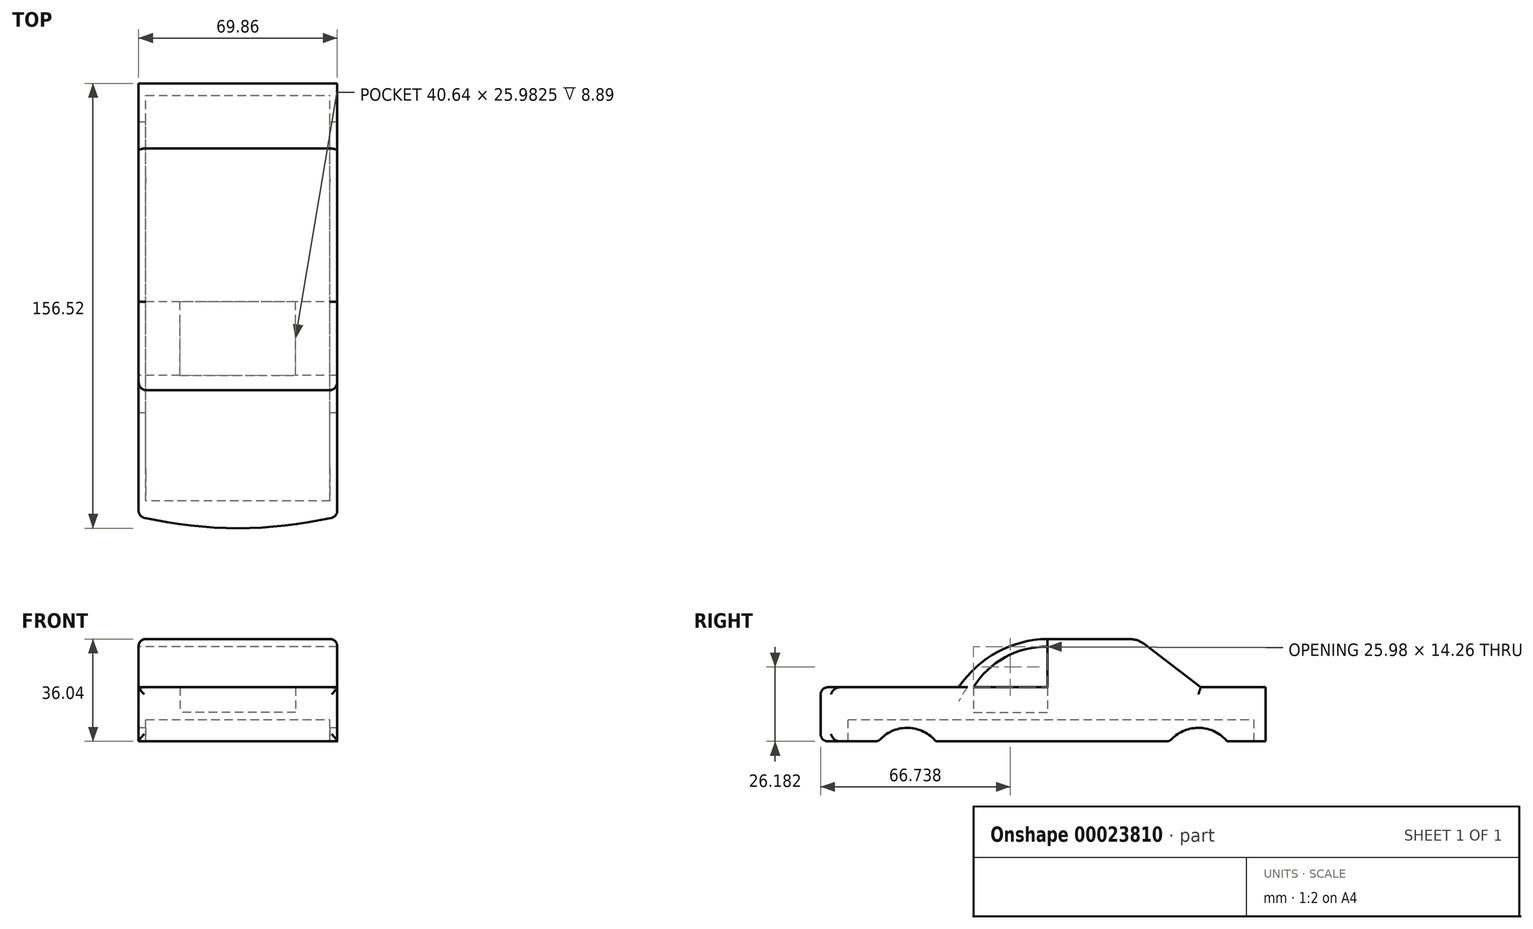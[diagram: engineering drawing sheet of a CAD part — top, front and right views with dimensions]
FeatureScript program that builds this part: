
annotation { "Feature Type Name" : "Feature", "Feature Type Description" : "" }
export const myFeature = defineFeature(function(context is Context, id is Id, definition is map)
    precondition{}
    {
        {
            var Q0;
            Q0=qCreatedBy(makeId("Top.planeOp"),FACE);
            var sketch = newSketch(context, id + "F0", { "sketchPlane" : qUnion([Q0])});
            skArc(sketch, "E0", {"start": v(-34.92, -38.6) * mm, "mid": v(0, -42.72) * mm, "end": v(34.93, -38.6) * mm});
            skPoint(sketch, "E1", {"position": v(0, -38.44) * mm});
            skLineSegment(sketch, "E2", {"start": v(-34.92, -38.6) * mm, "end": v(-34.92, 5.85) * mm});
            skLineSegment(sketch, "E3", {"start": v(-34.92, 5.85) * mm, "end": v(34.93, 5.85) * mm});
            skLineSegment(sketch, "E4", {"start": v(34.93, 5.85) * mm, "end": v(34.93, -38.6) * mm});
            skLineSegment(sketch, "E5", {"start": v(-76.26, -38.6) * mm, "end": v(76.46, -38.6) * mm, "construction": true});
            skSolve(sketch);
        }
        {
            var Q0;
            Q0 = qSketchRegion(id + "F0", true);
            extrude(context, id + "F1", {"entities" : qUnion([Q0]), "depth" : 6.35 * mm, "hasSecondDirection" : true, "secondDirectionOppositeDirection" : true, "secondDirectionDepth" : 12.7 * mm});
        }
        {
            var Q0;
            Q0=qCreatedBy(makeId("Right.planeOp"),FACE);
            var sketch = newSketch(context, id + "F2", { "sketchPlane" : qUnion([Q0])});
            skArc(sketch, "E6", {"start": v(37, 23.34) * mm, "mid": v(19.33, 18.7) * mm, "end": v(5.85, 6.35) * mm});
            skLineSegment(sketch, "E7", {"start": v(37, 23.34) * mm, "end": v(68.76, 23.34) * mm});
            skLineSegment(sketch, "E8", {"start": v(68.76, 23.34) * mm, "end": v(90.94, 6.35) * mm});
            skLineSegment(sketch, "E9", {"start": v(90.94, 6.35) * mm, "end": v(113.8, 6.35) * mm});
            skLineSegment(sketch, "E10", {"start": v(113.8, -12.7) * mm, "end": v(5.85, -12.7) * mm});
            skLineSegment(sketch, "E11", {"start": v(5.85, -12.7) * mm, "end": v(5.85, 6.35) * mm});
            skLineSegment(sketch, "E12", {"start": v(113.8, 6.35) * mm, "end": v(113.8, -12.7) * mm});
            skSolve(sketch);
        }
        {
            var Q0;
            Q0 = qSketchRegion(id + "F2", true);
            extrude(context, id + "F3", {"entities" : qUnion([Q0]), "operationType" : NewBodyOperationType.ADD, "depth" : 34.92 * mm, "hasSecondDirection" : true, "secondDirectionOppositeDirection" : true, "secondDirectionDepth" : 34.92 * mm});
        }
        {
            var Q0;
            Q0=makeQuery(id+"F3.opExtrude","CAP_FACE",FACE,{"disambiguationData":[OSD([sQuery(id+"F2.wireOp",EDGE,"E6"),sQuery(id+"F2.wireOp",EDGE,"E7"),sQuery(id+"F2.wireOp",EDGE,"E8"),sQuery(id+"F2.wireOp",EDGE,"E9"),sQuery(id+"F2.wireOp",EDGE,"E10"),sQuery(id+"F2.wireOp",EDGE,"E11"),sQuery(id+"F2.wireOp",EDGE,"E12")])],"isStart":true});
            var sketch = newSketch(context, id + "F4", { "sketchPlane" : qUnion([Q0])});
            skArc(sketch, "E13", {"start": v(-11.03, 6.35) * mm, "mid": v(-22.12, 16.93) * mm, "end": v(-37, 20.61) * mm});
            skLineSegment(sketch, "E14", {"start": v(-37, 20.61) * mm, "end": v(-37, 6.35) * mm});
            skLineSegment(sketch, "E15", {"start": v(-37, 6.35) * mm, "end": v(-11.03, 6.35) * mm});
            skSolve(sketch);
        }
        {
            var Q0;
            Q0 = qSketchRegion(id + "F4", true);
            extrude(context, id + "F5", {"entities" : qUnion([Q0]), "operationType" : NewBodyOperationType.REMOVE, "endBound" : BoundingType.THROUGH_ALL, "oppositeDirection" : true, "depth" : 25.4 * mm});
        }
        {
            var Q0;
            Q0=qCreatedBy(makeId("Right.planeOp"),FACE);
            var sketch = newSketch(context, id + "F6", { "sketchPlane" : qUnion([Q0])});
            skLineSegment(sketch, "E16.bottom", {"start": v(37, 6.35) * mm, "end": v(11.03, 6.35) * mm});
            skLineSegment(sketch, "E16.top", {"start": v(37, -8.9) * mm, "end": v(11.03, -8.9) * mm});
            skLineSegment(sketch, "E16.left", {"start": v(37, 6.35) * mm, "end": v(37, -8.9) * mm});
            skLineSegment(sketch, "E16.right", {"start": v(11.03, 6.35) * mm, "end": v(11.03, -8.9) * mm});
            skSolve(sketch);
        }
        {
            var Q0;
            Q0 = qSketchRegion(id + "F6", true);
            extrude(context, id + "F7", {"entities" : qUnion([Q0]), "operationType" : NewBodyOperationType.REMOVE, "oppositeDirection" : true, "depth" : 20.32 * mm, "hasSecondDirection" : true, "secondDirectionOppositeDirection" : false, "secondDirectionDepth" : 20.32 * mm});
        }
        {
            var Q0;
            Q0=makeQuery(id+"F3.opExtrude","CAP_FACE",FACE,{"disambiguationData":[OSD([sQuery(id+"F2.wireOp",EDGE,"E6"),sQuery(id+"F2.wireOp",EDGE,"E7"),sQuery(id+"F2.wireOp",EDGE,"E8"),sQuery(id+"F2.wireOp",EDGE,"E9"),sQuery(id+"F2.wireOp",EDGE,"E10"),sQuery(id+"F2.wireOp",EDGE,"E11"),sQuery(id+"F2.wireOp",EDGE,"E12")])],"isStart":true});
            var sketch = newSketch(context, id + "F8", { "sketchPlane" : qUnion([Q0])});
            skArc(sketch, "E17", {"start": v(-80.04, -12.7) * mm, "mid": v(-90.12, -7.94) * mm, "end": v(-100.2, -12.7) * mm});
            skSolve(sketch);
        }
        {
            var Q0;
            {var subQ1=sQuery(id+"F8.wireOp",EDGE,"E17");Q0=makeQuery(id+"F8.imprint","IMPRINT",FACE,{"disambiguationData":[TD([[makeQuery(id+"F8.imprint","IMPRINT",EDGE,{"derivedFrom":subQ1}),1.0]])]});}
            extrude(context, id + "F9", {"entities" : qUnion([Q0]), "operationType" : NewBodyOperationType.REMOVE, "endBound" : BoundingType.THROUGH_ALL, "oppositeDirection" : true, "depth" : 25.4 * mm});
        }
        {
            var Q0;
            Q0=makeQuery(id+"F1.opExtrude","SWEPT_FACE",FACE,{"disambiguationData":[OSD([sQuery(id+"F0.wireOp",EDGE,"E2")])]});
            var sketch = newSketch(context, id + "F10", { "sketchPlane" : qUnion([Q0])});
            skArc(sketch, "E18", {"start": v(22.36, -12.7) * mm, "mid": v(12.28, -7.94) * mm, "end": v(2.2, -12.7) * mm});
            skSolve(sketch);
        }
        {
            var Q0;
            {var subQ1=sQuery(id+"F10.wireOp",EDGE,"E18");Q0=makeQuery(id+"F10.imprint","IMPRINT",FACE,{"disambiguationData":[TD([[makeQuery(id+"F10.imprint","IMPRINT",EDGE,{"derivedFrom":subQ1}),1.0]])]});}
            extrude(context, id + "F11", {"entities" : qUnion([Q0]), "operationType" : NewBodyOperationType.REMOVE, "endBound" : BoundingType.THROUGH_ALL, "oppositeDirection" : true, "depth" : 25.4 * mm});
        }
        {
            var Q0;
            {var subQ0=sQuery(id+"F0.wireOp",EDGE,"E0");var subQ1=sQuery(id+"F0.wireOp",EDGE,"E2");var subQ2=sQuery(id+"F0.wireOp",EDGE,"E4");var subQ3=sQuery(id+"F2.wireOp",EDGE,"E10");var subQ4=makeQuery(id+"F9.opExtrude","SWEPT_FACE",FACE,{"disambiguationData":[OSD([sQuery(id+"F8.wireOp",EDGE,"E17")])]});Q0=makeQuery(id+"F11.boolean.opBoolean","SPLIT",FACE,{"disambiguationData":[TD([makeQuery(id+"F9.boolean.opBoolean","COPY",FACE,{"derivedFrom":subQ4})])],"derivedFrom":makeQuery(id+"F9.boolean.opBoolean","SPLIT",FACE,{"disambiguationData":[TD([makeQuery(id+"F1.opExtrude","SWEPT_FACE",FACE,{"disambiguationData":[OSD([subQ0])]})])],"derivedFrom":makeQuery(id+"F3.boolean.opBoolean","MERGE",FACE,{"derivedFrom":[makeQuery(id+"F1.opExtrude","CAP_FACE",FACE,{"disambiguationData":[OSD([subQ0,subQ1,sQuery(id+"F0.wireOp",EDGE,"E3"),subQ2])],"isStart":true}),makeQuery(id+"F3.opExtrude","SWEPT_FACE",FACE,{"disambiguationData":[OSD([subQ3])]})]})})});}
            var sketch = newSketch(context, id + "F12", { "sketchPlane" : qUnion([Q0])});
            skLineSegment(sketch, "E19.left", {"start": v(32.38, 5.25) * mm, "end": v(32.39, -83.09) * mm});
            skLineSegment(sketch, "E19.right", {"start": v(-32.39, 5.25) * mm, "end": v(-32.38, -83.09) * mm});
            skLineSegment(sketch, "E20", {"start": v(-32.39, 5.25) * mm, "end": v(32.38, 5.25) * mm});
            skLineSegment(sketch, "E21", {"start": v(-32.38, -83.09) * mm, "end": v(32.39, -83.09) * mm});
            skSolve(sketch);
        }
        {
            var Q0;
            Q0 = qSketchRegion(id + "F12", true);
            extrude(context, id + "F13", {"entities" : qUnion([Q0]), "operationType" : NewBodyOperationType.REMOVE, "oppositeDirection" : true, "depth" : 7.62 * mm});
        }
        {
            var Q0;
            Q0=makeQuery(id+"F3.opExtrude","CAP_EDGE",EDGE,{"disambiguationData":[OSD([sQuery(id+"F2.wireOp",EDGE,"E7")])],"isStart":true});
            var Q1;
            Q1=makeQuery(id+"F3.opExtrude","CAP_EDGE",EDGE,{"disambiguationData":[OSD([sQuery(id+"F2.wireOp",EDGE,"E7")])],"isStart":false});
            var Q2;
            Q2=makeQuery(id+"F3.opExtrude","CAP_EDGE",EDGE,{"disambiguationData":[OSD([sQuery(id+"F2.wireOp",EDGE,"E8")])],"isStart":false});
            var Q3;
            Q3=makeQuery(id+"F3.opExtrude","CAP_EDGE",EDGE,{"disambiguationData":[OSD([sQuery(id+"F2.wireOp",EDGE,"E8")])],"isStart":true});
            var Q4;
            Q4=makeQuery(id+"F3.opExtrude","CAP_EDGE",EDGE,{"disambiguationData":[OSD([sQuery(id+"F2.wireOp",EDGE,"E9")])],"isStart":true});
            var Q5;
            Q5=makeQuery(id+"F3.opExtrude","CAP_EDGE",EDGE,{"disambiguationData":[OSD([sQuery(id+"F2.wireOp",EDGE,"E9")])],"isStart":false});
            fillet(context, id + "F14", {"entities" : qUnion([Q0, Q1, Q2, Q3, Q4, Q5]), "radius" : 2.54 * mm, "tangentPropagation" : true, "allowEdgeOverflow" : false});
        }
        {
            var Q0;
            Q0=makeQuery(id+"F3.opExtrude","SWEPT_EDGE",EDGE,{"disambiguationData":[OSD([sQuery(id+"F2.wireOp",EDGE,"E7"),sQuery(id+"F2.wireOp",EDGE,"E8")])]});
            fillet(context, id + "F15", {"entities" : qUnion([Q0]), "radius" : 8.9 * mm, "tangentPropagation" : true, "allowEdgeOverflow" : false});
        }
        {
            var Q0;
            Q0=makeQuery(id+"F3.opExtrude","CAP_EDGE",EDGE,{"disambiguationData":[OSD([sQuery(id+"F2.wireOp",EDGE,"E6")])],"isStart":true});
            fillet(context, id + "F16", {"entities" : qUnion([Q0]), "radius" : 2.54 * mm, "tangentPropagation" : true, "allowEdgeOverflow" : false});
        }
        {
            var Q0;
            Q0=makeQuery(id+"F1.opExtrude","CAP_EDGE",EDGE,{"disambiguationData":[OSD([sQuery(id+"F0.wireOp",EDGE,"E0")])],"isStart":false});
            var Q1;
            Q1=makeQuery(id+"F1.opExtrude","SWEPT_EDGE",EDGE,{"disambiguationData":[OSD([sQuery(id+"F0.wireOp",EDGE,"E0"),sQuery(id+"F0.wireOp",EDGE,"E2")])]});
            var Q2;
            Q2=makeQuery(id+"F1.opExtrude","SWEPT_EDGE",EDGE,{"disambiguationData":[OSD([sQuery(id+"F0.wireOp",EDGE,"E0"),sQuery(id+"F0.wireOp",EDGE,"E4")])]});
            var Q3;
            Q3=makeQuery(id+"F1.opExtrude","CAP_EDGE",EDGE,{"disambiguationData":[OSD([sQuery(id+"F0.wireOp",EDGE,"E0")])],"isStart":true});
            var Q4;
            {var subQ0=sQuery(id+"F0.wireOp",EDGE,"E2");var subQ1=sQuery(id+"F10.wireOp",EDGE,"E18");Q4=makeQuery(id+"F11.boolean.opBoolean","COPY",EDGE,{"derivedFrom":makeQuery(id+"F11.opExtrude","SWEPT_EDGE",EDGE,{"disambiguationData":[OSD([subQ0,subQ1]),TDD([makeQuery(id+"F10.imprint","INTERSECT",VERTEX,{"disambiguationData":[OD(0.0)],"derivedFrom":[makeQuery(id+"F1.opExtrude","CAP_EDGE",EDGE,{"disambiguationData":[OSD([subQ0])],"isStart":true}),subQ1]})])]})});}
            var Q5;
            Q5=makeQuery(id+"F13.boolean.opBoolean","INTERSECT",EDGE,{"derivedFrom":[makeQuery(id+"F11.boolean.opBoolean","COPY",FACE,{"derivedFrom":makeQuery(id+"F11.opExtrude","SWEPT_FACE",FACE,{"disambiguationData":[OSD([sQuery(id+"F10.wireOp",EDGE,"E18")])]})}),makeQuery(id+"F13.opExtrude","SWEPT_FACE",FACE,{"disambiguationData":[OSD([sQuery(id+"F12.wireOp",EDGE,"E20")])]})]});
            var Q6;
            Q6=makeQuery(id+"F13.boolean.opBoolean","INTERSECT",EDGE,{"derivedFrom":[makeQuery(id+"F9.boolean.opBoolean","COPY",FACE,{"derivedFrom":makeQuery(id+"F9.opExtrude","SWEPT_FACE",FACE,{"disambiguationData":[OSD([sQuery(id+"F8.wireOp",EDGE,"E17")])]})}),makeQuery(id+"F13.opExtrude","SWEPT_FACE",FACE,{"disambiguationData":[OSD([sQuery(id+"F12.wireOp",EDGE,"E21")])]})]});
            var Q7;
            {var subQ0=sQuery(id+"F2.wireOp",EDGE,"E10");var subQ1=sQuery(id+"F8.wireOp",EDGE,"E17");Q7=makeQuery(id+"F9.boolean.opBoolean","COPY",EDGE,{"derivedFrom":makeQuery(id+"F9.opExtrude","SWEPT_EDGE",EDGE,{"disambiguationData":[OSD([subQ0,subQ1]),TDD([makeQuery(id+"F8.imprint","INTERSECT",VERTEX,{"disambiguationData":[OD(1.0)],"derivedFrom":[makeQuery(id+"F3.opExtrude","CAP_EDGE",EDGE,{"disambiguationData":[OSD([subQ0])],"isStart":true}),subQ1]})])]})});}
            fillet(context, id + "F17", {"entities" : qUnion([Q0, Q1, Q2, Q3, Q4, Q5, Q6, Q7]), "radius" : 2.54 * mm, "tangentPropagation" : true, "allowEdgeOverflow" : false});
        }
        {
            var Q0;
            Q0=makeQuery(id+"F13.boolean.opBoolean","COPY",FACE,{"derivedFrom":makeQuery(id+"F13.opExtrude","CAP_FACE",FACE,{"disambiguationData":[OSD([sQuery(id+"F12.wireOp",EDGE,"E19.left"),sQuery(id+"F12.wireOp",EDGE,"E19.right"),sQuery(id+"F12.wireOp",EDGE,"E20"),sQuery(id+"F12.wireOp",EDGE,"E21")])],"isStart":false})});
            var sketch = newSketch(context, id + "F18", { "sketchPlane" : qUnion([Q0])});
            skLineSegment(sketch, "E22.bottom", {"start": v(20.32, -37) * mm, "end": v(-20.32, -37) * mm});
            skLineSegment(sketch, "E22.top", {"start": v(20.32, -11.03) * mm, "end": v(-20.32, -11.03) * mm});
            skLineSegment(sketch, "E22.left", {"start": v(20.32, -37) * mm, "end": v(20.32, -11.03) * mm});
            skLineSegment(sketch, "E22.right", {"start": v(-20.32, -37) * mm, "end": v(-20.32, -11.03) * mm});
            skSolve(sketch);
        }
        {
            var Q0;
            Q0 = qSketchRegion(id + "F18", true);
            extrude(context, id + "F19", {"entities" : qUnion([Q0]), "operationType" : NewBodyOperationType.ADD, "oppositeDirection" : true, "depth" : 2.54 * mm});
        }
        {
            var Q0;
            Q0=makeQuery(id+"F19.boolean.opBoolean","MERGE",FACE,{"derivedFrom":[makeQuery(id+"F13.boolean.opBoolean","COPY",FACE,{"derivedFrom":makeQuery(id+"F13.opExtrude","CAP_FACE",FACE,{"disambiguationData":[OSD([sQuery(id+"F12.wireOp",EDGE,"E19.left"),sQuery(id+"F12.wireOp",EDGE,"E19.right"),sQuery(id+"F12.wireOp",EDGE,"E20"),sQuery(id+"F12.wireOp",EDGE,"E21")])],"isStart":false})}),makeQuery(id+"F19.opExtrude","CAP_FACE",FACE,{"disambiguationData":[OSD([sQuery(id+"F18.wireOp",EDGE,"E22.bottom"),sQuery(id+"F18.wireOp",EDGE,"E22.top"),sQuery(id+"F18.wireOp",EDGE,"E22.left"),sQuery(id+"F18.wireOp",EDGE,"E22.right")])],"isStart":true})]});
            var sketch = newSketch(context, id + "F20", { "sketchPlane" : qUnion([Q0])});
            skLineSegment(sketch, "E23.bottom", {"start": v(-32.39, 21.67) * mm, "end": v(32.38, 21.67) * mm});
            skLineSegment(sketch, "E23.top", {"start": v(-32.39, -99.5) * mm, "end": v(32.38, -99.5) * mm});
            skLineSegment(sketch, "E23.left", {"start": v(-32.39, 21.67) * mm, "end": v(-32.39, -99.5) * mm});
            skLineSegment(sketch, "E23.right", {"start": v(32.38, 21.67) * mm, "end": v(32.38, -99.5) * mm});
            skSolve(sketch);
        }
        {
            var Q0;
            Q0 = qSketchRegion(id + "F20", true);
            extrude(context, id + "F21", {"entities" : qUnion([Q0]), "operationType" : NewBodyOperationType.REMOVE, "depth" : 25.4 * mm});
        }
        {
            var Q0;
            Q0=makeQuery(id+"F21.boolean.opBoolean","COPY",FACE,{"derivedFrom":makeQuery(id+"F21.opExtrude","SWEPT_FACE",FACE,{"disambiguationData":[OSD([sQuery(id+"F20.wireOp",EDGE,"E23.top")])]})});
            var sketch = newSketch(context, id + "F22", { "sketchPlane" : qUnion([Q0])});
            skLineSegment(sketch, "E24.bottom", {"start": v(-32.39, -5.08) * mm, "end": v(32.38, -5.08) * mm});
            skLineSegment(sketch, "E24.top", {"start": v(-32.39, -15.16) * mm, "end": v(32.38, -15.16) * mm});
            skLineSegment(sketch, "E24.left", {"start": v(-32.39, -5.08) * mm, "end": v(-32.39, -15.16) * mm});
            skLineSegment(sketch, "E24.right", {"start": v(32.38, -5.08) * mm, "end": v(32.38, -15.16) * mm});
            skSolve(sketch);
        }
        {
            var Q0;
            Q0 = qSketchRegion(id + "F22", true);
            extrude(context, id + "F23", {"entities" : qUnion([Q0]), "operationType" : NewBodyOperationType.REMOVE, "oppositeDirection" : true, "depth" : 10.16 * mm});
        }
        {
            var Q0;
            Q0=makeQuery(id+"F21.boolean.opBoolean","COPY",FACE,{"derivedFrom":makeQuery(id+"F21.opExtrude","SWEPT_FACE",FACE,{"disambiguationData":[OSD([sQuery(id+"F20.wireOp",EDGE,"E23.bottom")])]})});
            var sketch = newSketch(context, id + "F24", { "sketchPlane" : qUnion([Q0])});
            skLineSegment(sketch, "E25.bottom", {"start": v(-32.38, -5.08) * mm, "end": v(32.39, -5.08) * mm});
            skLineSegment(sketch, "E25.top", {"start": v(-32.38, -17.37) * mm, "end": v(32.39, -17.37) * mm});
            skLineSegment(sketch, "E25.left", {"start": v(-32.38, -5.08) * mm, "end": v(-32.38, -17.37) * mm});
            skLineSegment(sketch, "E25.right", {"start": v(32.39, -5.08) * mm, "end": v(32.39, -17.37) * mm});
            skSolve(sketch);
        }
        {
            var Q0;
            Q0 = qSketchRegion(id + "F24", true);
            extrude(context, id + "F25", {"entities" : qUnion([Q0]), "operationType" : NewBodyOperationType.REMOVE, "oppositeDirection" : true, "depth" : 11.43 * mm});
        }
        {
            var Q0;
            {var subQ0=sQuery(id+"F0.wireOp",EDGE,"E2");var subQ1=sQuery(id+"F10.wireOp",EDGE,"E18");var subQ2=sQuery(id+"F0.wireOp",EDGE,"E4");Q0=makeQuery(id+"F13.boolean.opBoolean","SPLIT",EDGE,{"disambiguationData":[TD([makeQuery(id+"F1.opExtrude","SWEPT_FACE",FACE,{"disambiguationData":[OSD([subQ2])]})])],"derivedFrom":makeQuery(id+"F11.boolean.opBoolean","COPY",EDGE,{"derivedFrom":makeQuery(id+"F11.opExtrude","SWEPT_EDGE",EDGE,{"disambiguationData":[OSD([subQ0,subQ1]),TDD([makeQuery(id+"F10.imprint","INTERSECT",VERTEX,{"disambiguationData":[OD(1.0)],"derivedFrom":[makeQuery(id+"F1.opExtrude","CAP_EDGE",EDGE,{"disambiguationData":[OSD([subQ0])],"isStart":true}),subQ1]})])]})})});}
            var Q1;
            {var subQ0=sQuery(id+"F2.wireOp",EDGE,"E10");var subQ1=sQuery(id+"F8.wireOp",EDGE,"E17");Q1=makeQuery(id+"F13.boolean.opBoolean","SPLIT",EDGE,{"disambiguationData":[TD([makeQuery(id+"F13.opExtrude","SWEPT_FACE",FACE,{"disambiguationData":[OSD([sQuery(id+"F12.wireOp",EDGE,"E19.left")])]})])],"derivedFrom":makeQuery(id+"F9.boolean.opBoolean","COPY",EDGE,{"derivedFrom":makeQuery(id+"F9.opExtrude","SWEPT_EDGE",EDGE,{"disambiguationData":[OSD([subQ0,subQ1]),TDD([makeQuery(id+"F8.imprint","INTERSECT",VERTEX,{"disambiguationData":[OD(0.0)],"derivedFrom":[makeQuery(id+"F3.opExtrude","CAP_EDGE",EDGE,{"disambiguationData":[OSD([subQ0])],"isStart":true}),subQ1]})])]})})});}
            var Q2;
            {var subQ0=sQuery(id+"F0.wireOp",EDGE,"E2");var subQ1=sQuery(id+"F10.wireOp",EDGE,"E18");Q2=makeQuery(id+"F13.boolean.opBoolean","SPLIT",EDGE,{"disambiguationData":[TD([makeQuery(id+"F1.opExtrude","SWEPT_FACE",FACE,{"disambiguationData":[OSD([subQ0])]})])],"derivedFrom":makeQuery(id+"F11.boolean.opBoolean","COPY",EDGE,{"derivedFrom":makeQuery(id+"F11.opExtrude","SWEPT_EDGE",EDGE,{"disambiguationData":[OSD([subQ0,subQ1]),TDD([makeQuery(id+"F10.imprint","INTERSECT",VERTEX,{"disambiguationData":[OD(1.0)],"derivedFrom":[makeQuery(id+"F1.opExtrude","CAP_EDGE",EDGE,{"disambiguationData":[OSD([subQ0])],"isStart":true}),subQ1]})])]})})});}
            var Q3;
            {var subQ0=sQuery(id+"F2.wireOp",EDGE,"E10");var subQ1=sQuery(id+"F8.wireOp",EDGE,"E17");Q3=makeQuery(id+"F13.boolean.opBoolean","SPLIT",EDGE,{"disambiguationData":[TD([makeQuery(id+"F13.opExtrude","SWEPT_FACE",FACE,{"disambiguationData":[OSD([sQuery(id+"F12.wireOp",EDGE,"E19.right")])]})])],"derivedFrom":makeQuery(id+"F9.boolean.opBoolean","COPY",EDGE,{"derivedFrom":makeQuery(id+"F9.opExtrude","SWEPT_EDGE",EDGE,{"disambiguationData":[OSD([subQ0,subQ1]),TDD([makeQuery(id+"F8.imprint","INTERSECT",VERTEX,{"disambiguationData":[OD(0.0)],"derivedFrom":[makeQuery(id+"F3.opExtrude","CAP_EDGE",EDGE,{"disambiguationData":[OSD([subQ0])],"isStart":true}),subQ1]})])]})})});}
            fillet(context, id + "F26", {"entities" : qUnion([Q0, Q1, Q2, Q3]), "radius" : 2.54 * mm, "tangentPropagation" : true, "allowEdgeOverflow" : false});
        }
    });
